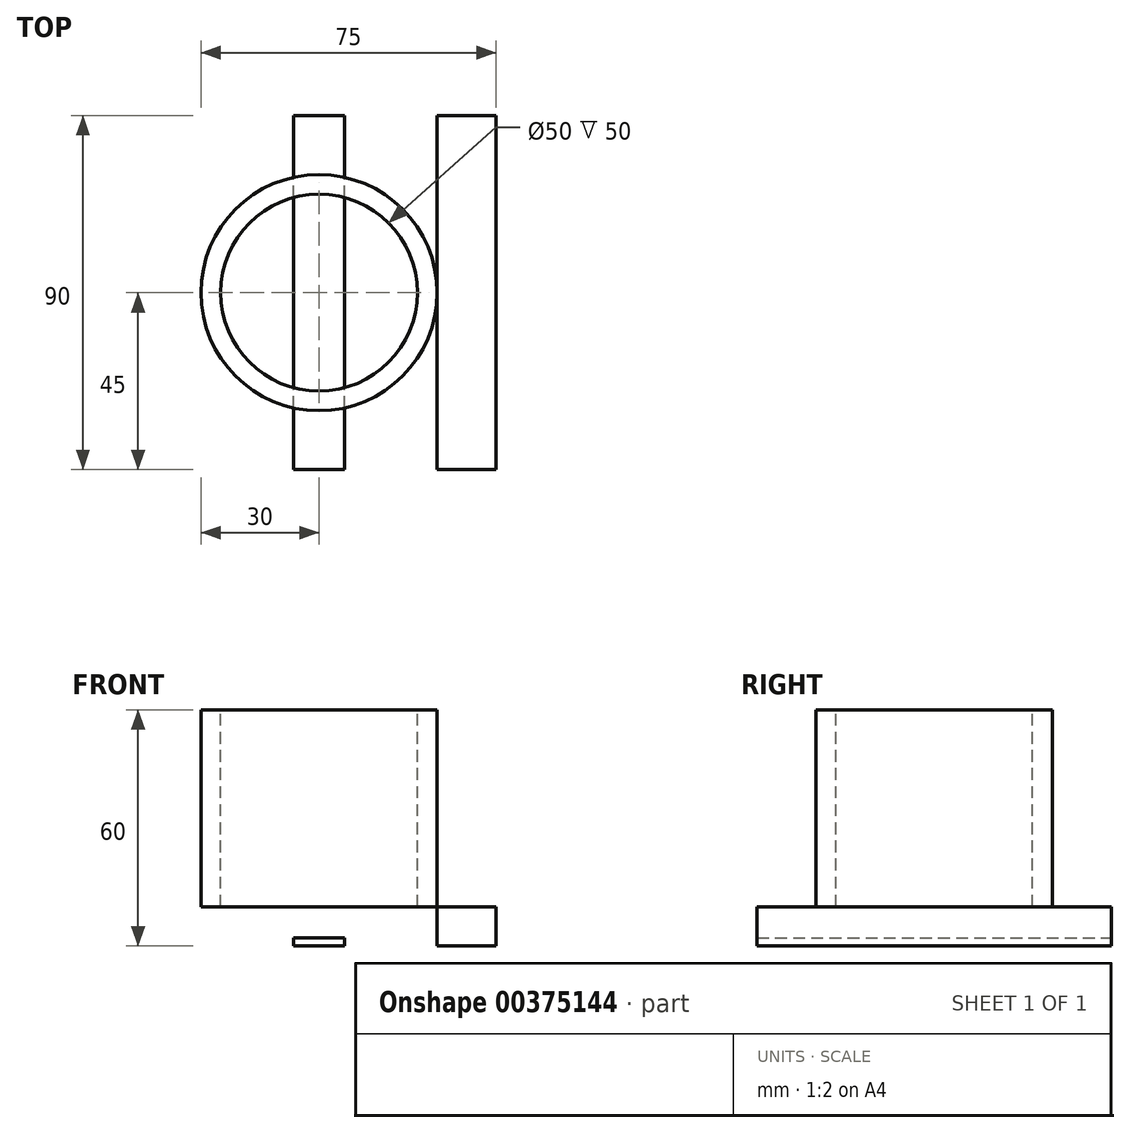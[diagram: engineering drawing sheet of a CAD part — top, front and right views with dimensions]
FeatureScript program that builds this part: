
annotation { "Feature Type Name" : "Feature", "Feature Type Description" : "" }
export const myFeature = defineFeature(function(context is Context, id is Id, definition is map)
    precondition{}
    {
        {
            var Q0;
            Q0=qCreatedBy(makeId("Front.planeOp"),FACE);
            var sketch = newSketch(context, id + "F0", { "sketchPlane" : qUnion([Q0])});
            skLineSegment(sketch, "E0.bottom", {"start": v(-30, 0) * mm, "end": v(-25, 0) * mm});
            skLineSegment(sketch, "E0.top", {"start": v(-30, 50) * mm, "end": v(-25, 50) * mm});
            skLineSegment(sketch, "E0.left", {"start": v(-30, 0) * mm, "end": v(-30, 50) * mm});
            skLineSegment(sketch, "E0.right", {"start": v(-25, 0) * mm, "end": v(-25, 50) * mm});
            skLineSegment(sketch, "E1.bottom", {"start": v(-30, 0) * mm, "end": v(0, 0) * mm});
            skLineSegment(sketch, "E1.top", {"start": v(-30, -10) * mm, "end": v(0, -10) * mm});
            skLineSegment(sketch, "E1.right", {"start": v(0, 0) * mm, "end": v(0, -10) * mm});
            skLineSegment(sketch, "E2.bottom", {"start": v(0, -10) * mm, "end": v(-6.5, -10) * mm});
            skLineSegment(sketch, "E2.top", {"start": v(0, -8) * mm, "end": v(-6.5, -8) * mm});
            skLineSegment(sketch, "E2.left", {"start": v(0, -10) * mm, "end": v(0, -8) * mm});
            skLineSegment(sketch, "E2.right", {"start": v(-6.5, -10) * mm, "end": v(-6.5, -8) * mm});
            skLineSegment(sketch, "E3.bottom", {"start": v(0, -8) * mm, "end": v(-4.5, -8) * mm});
            skLineSegment(sketch, "E3.top", {"start": v(0, -4) * mm, "end": v(-4.5, -4) * mm});
            skLineSegment(sketch, "E3.left", {"start": v(0, -8) * mm, "end": v(0, -4) * mm});
            skLineSegment(sketch, "E3.right", {"start": v(-4.5, -8) * mm, "end": v(-4.5, -4) * mm});
            skLineSegment(sketch, "E4", {"start": v(-4.5, -4) * mm, "end": v(-10, 0) * mm});
            skLineSegment(sketch, "E5.bottom", {"start": v(-30, 0) * mm, "end": v(-45, 0) * mm});
            skLineSegment(sketch, "E5.top", {"start": v(-30, -10) * mm, "end": v(-45, -10) * mm});
            skLineSegment(sketch, "E5.right", {"start": v(-45, 0) * mm, "end": v(-45, -10) * mm});
            skLineSegment(sketch, "E6.bottom", {"start": v(0, 0) * mm, "end": v(30, 0) * mm});
            skLineSegment(sketch, "E6.top", {"start": v(0, -10) * mm, "end": v(30, -10) * mm});
            skLineSegment(sketch, "E6.right", {"start": v(30, 0) * mm, "end": v(30, -10) * mm});
            skLineSegment(sketch, "E7.bottom", {"start": v(30, 0) * mm, "end": v(25, 0) * mm});
            skLineSegment(sketch, "E7.top", {"start": v(30, 48.8) * mm, "end": v(25, 48.8) * mm});
            skLineSegment(sketch, "E7.left", {"start": v(30, 0) * mm, "end": v(30, 48.8) * mm});
            skLineSegment(sketch, "E7.right", {"start": v(25, 0) * mm, "end": v(25, 48.8) * mm});
            skLineSegment(sketch, "E8.bottom", {"start": v(0, -4) * mm, "end": v(4.5, -4) * mm});
            skLineSegment(sketch, "E8.top", {"start": v(0, -8) * mm, "end": v(4.5, -8) * mm});
            skLineSegment(sketch, "E8.left", {"start": v(0, -4) * mm, "end": v(0, -8) * mm});
            skLineSegment(sketch, "E8.right", {"start": v(4.5, -4) * mm, "end": v(4.5, -8) * mm});
            skLineSegment(sketch, "E9.bottom", {"start": v(0, -10) * mm, "end": v(6.5, -10) * mm});
            skLineSegment(sketch, "E9.top", {"start": v(0, -8) * mm, "end": v(6.5, -8) * mm});
            skLineSegment(sketch, "E9.right", {"start": v(6.5, -10) * mm, "end": v(6.5, -8) * mm});
            skLineSegment(sketch, "E10.bottom", {"start": v(30, 0) * mm, "end": v(45, 0) * mm});
            skLineSegment(sketch, "E10.top", {"start": v(30, -10) * mm, "end": v(45, -10) * mm});
            skLineSegment(sketch, "E10.right", {"start": v(45, 0) * mm, "end": v(45, -10) * mm});
            skLineSegment(sketch, "E11", {"start": v(4.5, -4) * mm, "end": v(10, 0) * mm});
            skSolve(sketch);
        }
        {
            var Q0;
            Q0=makeQuery(id+"F0.imprint","IMPRINT",FACE,{"disambiguationData":[TD([[makeQuery(id+"F0.imprint","IMPRINT",EDGE,{"derivedFrom":sQuery(id+"F0.wireOp",EDGE,"E0.top")}),-1.0]])]});
            var Q1;
            Q1=makeQuery(id+"F0.imprint","IMPRINT",FACE,{"disambiguationData":[TD([[makeQuery(id+"F0.imprint","IMPRINT",EDGE,{"derivedFrom":sQuery(id+"F0.wireOp",EDGE,"E1.top")}),1.0]])]});
            var Q2;
            Q2=sQuery(id+"F0.wireOp",EDGE,"E1.right");
            revolve(context, id + "F1", {"entities" : qUnion([Q0, Q1]), "axis" : qUnion([Q2]), "revolveType" : RevolveType.FULL});
        }
        {
            var Q0;
            Q0=makeQuery(id+"F0.imprint","IMPRINT",FACE,{"disambiguationData":[TD([[makeQuery(id+"F0.imprint","IMPRINT",EDGE,{"derivedFrom":sQuery(id+"F0.wireOp",EDGE,"E1.top")}),1.0]])]});
            var Q1;
            Q1=makeQuery(id+"F0.imprint","IMPRINT",FACE,{"disambiguationData":[TD([[makeQuery(id+"F0.imprint","IMPRINT",EDGE,{"derivedFrom":sQuery(id+"F0.wireOp",EDGE,"E6.top")}),1.0]])]});
            var Q2;
            Q2=makeQuery(id+"F0.imprint","IMPRINT",FACE,{"disambiguationData":[TD([[makeQuery(id+"F0.imprint","IMPRINT",EDGE,{"derivedFrom":sQuery(id+"F0.wireOp",EDGE,"E10.bottom")}),-1.0]])]});
            extrude(context, id + "F2", {"entities" : qUnion([Q0, Q1, Q2]), "operationType" : NewBodyOperationType.ADD, "endBound" : BoundingType.SYMMETRIC, "depth" : 90 * mm});
        }
    });
